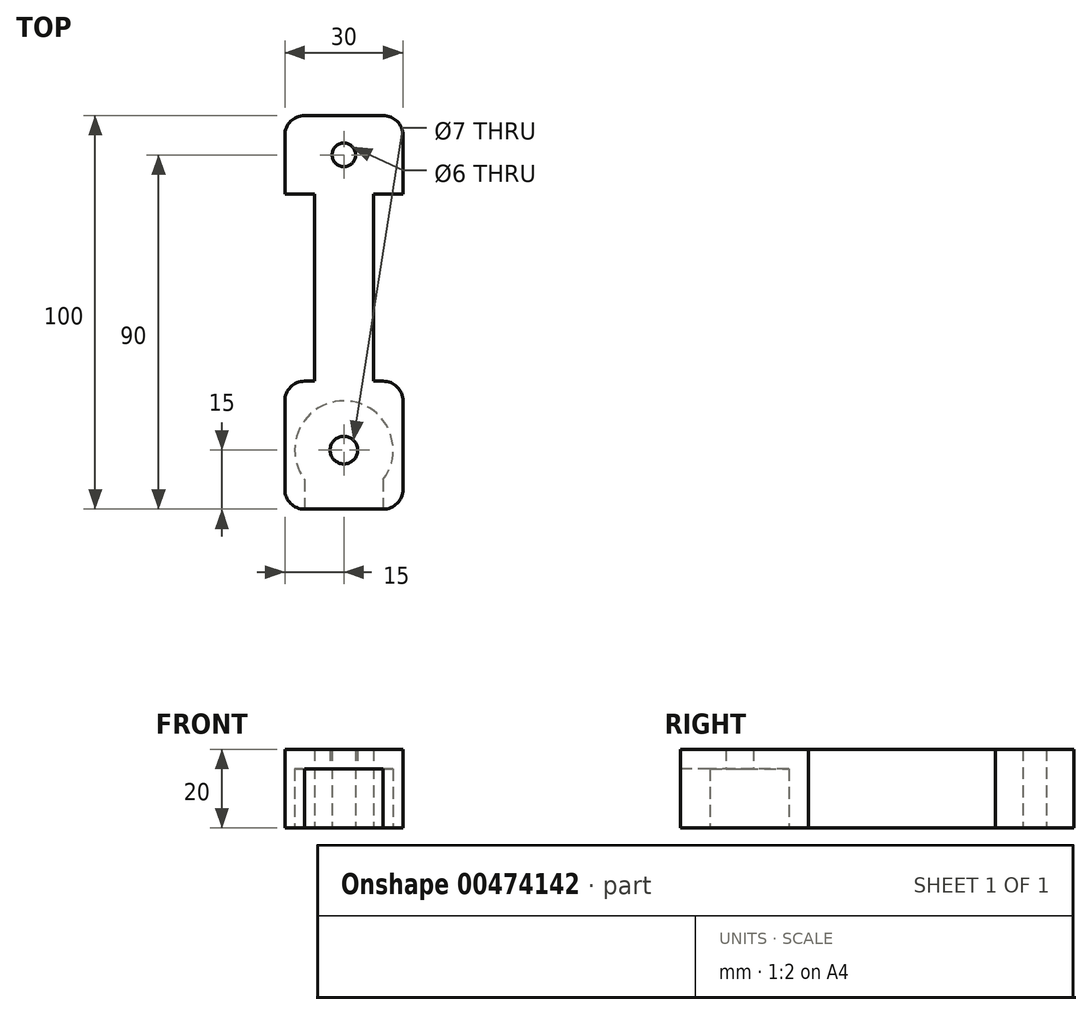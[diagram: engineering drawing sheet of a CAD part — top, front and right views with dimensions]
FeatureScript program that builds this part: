
annotation { "Feature Type Name" : "Feature", "Feature Type Description" : "" }
export const myFeature = defineFeature(function(context is Context, id is Id, definition is map)
    precondition{}
    {
        {
            var Q0;
            Q0=qCreatedBy(makeId("Top.planeOp"),FACE);
            var sketch = newSketch(context, id + "F0", { "sketchPlane" : qUnion([Q0])});
            skLineSegment(sketch, "E0.bottom", {"start": v(0, 0) * mm, "end": v(30, 0) * mm});
            skLineSegment(sketch, "E0.top", {"start": v(0, 100) * mm, "end": v(30, 100) * mm});
            skLineSegment(sketch, "E0.left", {"start": v(0, 0) * mm, "end": v(0, 100) * mm});
            skLineSegment(sketch, "E0.right", {"start": v(30, 0) * mm, "end": v(30, 100) * mm});
            skSolve(sketch);
        }
        {
            var Q0;
            Q0=makeQuery(id+"F0.imprint","IMPRINT",FACE,{"disambiguationData":[TD([[makeQuery(id+"F0.imprint","IMPRINT",EDGE,{"derivedFrom":sQuery(id+"F0.wireOp",EDGE,"E0.bottom")}),1.0]])]});
            extrude(context, id + "F1", {"entities" : qUnion([Q0]), "depth" : 20 * mm});
        }
        {
            var Q0;
            Q0=qCreatedBy(makeId("Top.planeOp"),FACE);
            var sketch = newSketch(context, id + "F2", { "sketchPlane" : qUnion([Q0])});
            skCircle(sketch, "E1", {"center": v(15, 15) * mm, "radius": 12.5 * mm});
            skSolve(sketch);
        }
        {
            var Q0;
            Q0=makeQuery(id+"F2.imprint","IMPRINT",FACE,{"disambiguationData":[TD([[makeQuery(id+"F2.imprint","IMPRINT",EDGE,{"derivedFrom":sQuery(id+"F2.wireOp",EDGE,"E1")}),1.0]])]});
            var Q1;
            Q1=sQuery(id+"F2.wireOp",EDGE,"E1");
            extrude(context, id + "F3", {"entities" : qUnion([Q0]), "operationType" : NewBodyOperationType.REMOVE, "surfaceEntities" : qUnion([Q1]), "depth" : 15 * mm});
        }
        {
            var Q0;
            Q0=qCreatedBy(makeId("Top.planeOp"),FACE);
            var sketch = newSketch(context, id + "F4", { "sketchPlane" : qUnion([Q0])});
            skCircle(sketch, "E2", {"center": v(15, 15) * mm, "radius": 3.5 * mm});
            skSolve(sketch);
        }
        {
            var Q0;
            Q0=makeQuery(id+"F4.imprint","IMPRINT",FACE,{"disambiguationData":[TD([[makeQuery(id+"F4.imprint","IMPRINT",EDGE,{"derivedFrom":sQuery(id+"F4.wireOp",EDGE,"E2")}),1.0]])]});
            extrude(context, id + "F5", {"entities" : qUnion([Q0]), "operationType" : NewBodyOperationType.REMOVE, "depth" : 20 * mm});
        }
        {
            var Q0;
            Q0=qCreatedBy(makeId("Top.planeOp"),FACE);
            var sketch = newSketch(context, id + "F6", { "sketchPlane" : qUnion([Q0])});
            skCircle(sketch, "E3", {"center": v(15, 90) * mm, "radius": 3 * mm});
            skSolve(sketch);
        }
        {
            var Q0;
            Q0=makeQuery(id+"F6.imprint","IMPRINT",FACE,{"disambiguationData":[TD([[makeQuery(id+"F6.imprint","IMPRINT",EDGE,{"derivedFrom":sQuery(id+"F6.wireOp",EDGE,"E3")}),1.0]])]});
            var Q1;
            Q1=sQuery(id+"F6.wireOp",EDGE,"E3");
            extrude(context, id + "F7", {"entities" : qUnion([Q0]), "operationType" : NewBodyOperationType.REMOVE, "surfaceEntities" : qUnion([Q1]), "depth" : 20 * mm});
        }
        {
            var Q0;
            Q0=qCreatedBy(makeId("Top.planeOp"),FACE);
            var sketch = newSketch(context, id + "F8", { "sketchPlane" : qUnion([Q0])});
            skLineSegment(sketch, "E4.bottom", {"start": v(0, 80) * mm, "end": v(7.5, 80) * mm});
            skLineSegment(sketch, "E4.top", {"start": v(0, 32.5) * mm, "end": v(7.5, 32.5) * mm});
            skLineSegment(sketch, "E4.left", {"start": v(0, 80) * mm, "end": v(0, 32.5) * mm});
            skLineSegment(sketch, "E4.right", {"start": v(7.5, 80) * mm, "end": v(7.5, 32.5) * mm});
            skSolve(sketch);
        }
        {
            var Q0;
            Q0 = qSketchRegion(id + "F8", true);
            extrude(context, id + "F9", {"entities" : qUnion([Q0]), "operationType" : NewBodyOperationType.REMOVE, "depth" : 20 * mm});
        }
        {
            var Q0;
            Q0=qCreatedBy(makeId("Top.planeOp"),FACE);
            var sketch = newSketch(context, id + "F10", { "sketchPlane" : qUnion([Q0])});
            skLineSegment(sketch, "E5.bottom", {"start": v(30, 32.5) * mm, "end": v(22.5, 32.5) * mm});
            skLineSegment(sketch, "E5.top", {"start": v(30, 80) * mm, "end": v(22.5, 80) * mm});
            skLineSegment(sketch, "E5.left", {"start": v(30, 32.5) * mm, "end": v(30, 80) * mm});
            skLineSegment(sketch, "E5.right", {"start": v(22.5, 32.5) * mm, "end": v(22.5, 80) * mm});
            skSolve(sketch);
        }
        {
            var Q0;
            Q0 = qSketchRegion(id + "F10", true);
            extrude(context, id + "F11", {"entities" : qUnion([Q0]), "operationType" : NewBodyOperationType.REMOVE, "depth" : 20 * mm});
        }
        {
            var Q0;
            Q0=makeQuery(id+"F11.boolean.opBoolean","COPY",EDGE,{"derivedFrom":makeQuery(id+"F11.opExtrude","SWEPT_EDGE",EDGE,{"disambiguationData":[OSD([sQuery(id+"F10.wireOp",EDGE,"E5.bottom"),sQuery(id+"F10.wireOp",EDGE,"E5.left")])]})});
            var Q1;
            Q1=makeQuery(id+"F1.opExtrude","SWEPT_EDGE",EDGE,{"disambiguationData":[OSD([sQuery(id+"F0.wireOp",EDGE,"E0.bottom"),sQuery(id+"F0.wireOp",EDGE,"E0.right")])]});
            var Q2;
            Q2=makeQuery(id+"F1.opExtrude","SWEPT_EDGE",EDGE,{"disambiguationData":[OSD([sQuery(id+"F0.wireOp",EDGE,"E0.bottom"),sQuery(id+"F0.wireOp",EDGE,"E0.left")])]});
            var Q3;
            Q3=makeQuery(id+"F9.boolean.opBoolean","COPY",EDGE,{"derivedFrom":makeQuery(id+"F9.opExtrude","SWEPT_EDGE",EDGE,{"disambiguationData":[OSD([sQuery(id+"F8.wireOp",EDGE,"E4.top"),sQuery(id+"F8.wireOp",EDGE,"E4.left")])]})});
            fillet(context, id + "F12", {"entities" : qUnion([Q0, Q1, Q2, Q3]), "radius" : 5 * mm, "tangentPropagation" : true, "allowEdgeOverflow" : false});
        }
        {
            var Q0;
            Q0=makeQuery(id+"F1.opExtrude","SWEPT_EDGE",EDGE,{"disambiguationData":[OSD([sQuery(id+"F0.wireOp",EDGE,"E0.top"),sQuery(id+"F0.wireOp",EDGE,"E0.left")])]});
            var Q1;
            Q1=makeQuery(id+"F9.boolean.opBoolean","COPY",EDGE,{"derivedFrom":makeQuery(id+"F9.opExtrude","SWEPT_EDGE",EDGE,{"disambiguationData":[OSD([sQuery(id+"F8.wireOp",EDGE,"E4.bottom"),sQuery(id+"F8.wireOp",EDGE,"E4.left")])]})});
            var Q2;
            Q2=makeQuery(id+"F1.opExtrude","SWEPT_EDGE",EDGE,{"disambiguationData":[OSD([sQuery(id+"F0.wireOp",EDGE,"E0.top"),sQuery(id+"F0.wireOp",EDGE,"E0.right")])]});
            var Q3;
            Q3=makeQuery(id+"F11.boolean.opBoolean","COPY",EDGE,{"derivedFrom":makeQuery(id+"F11.opExtrude","SWEPT_EDGE",EDGE,{"disambiguationData":[OSD([sQuery(id+"F10.wireOp",EDGE,"E5.top"),sQuery(id+"F10.wireOp",EDGE,"E5.left")])]})});
            fillet(context, id + "F13", {"entities" : qUnion([Q0, Q1, Q2, Q3]), "radius" : 5 * mm, "tangentPropagation" : true, "allowEdgeOverflow" : false});
        }
        {
            var Q0;
            Q0=qCreatedBy(makeId("Top.planeOp"),FACE);
            var sketch = newSketch(context, id + "F14", { "sketchPlane" : qUnion([Q0])});
            skLineSegment(sketch, "E6.bottom", {"start": v(25, 15) * mm, "end": v(5, 15) * mm});
            skLineSegment(sketch, "E6.top", {"start": v(25, 0) * mm, "end": v(5, 0) * mm});
            skLineSegment(sketch, "E6.left", {"start": v(25, 15) * mm, "end": v(25, 0) * mm});
            skLineSegment(sketch, "E6.right", {"start": v(5, 15) * mm, "end": v(5, 0) * mm});
            skSolve(sketch);
        }
        {
            var Q0;
            Q0=makeQuery(id+"F14.imprint","IMPRINT",FACE,{"disambiguationData":[TD([[makeQuery(id+"F14.imprint","IMPRINT",EDGE,{"derivedFrom":sQuery(id+"F14.wireOp",EDGE,"E6.bottom")}),1.0]])]});
            extrude(context, id + "F15", {"entities" : qUnion([Q0]), "operationType" : NewBodyOperationType.REMOVE, "depth" : 15 * mm});
        }
    });
